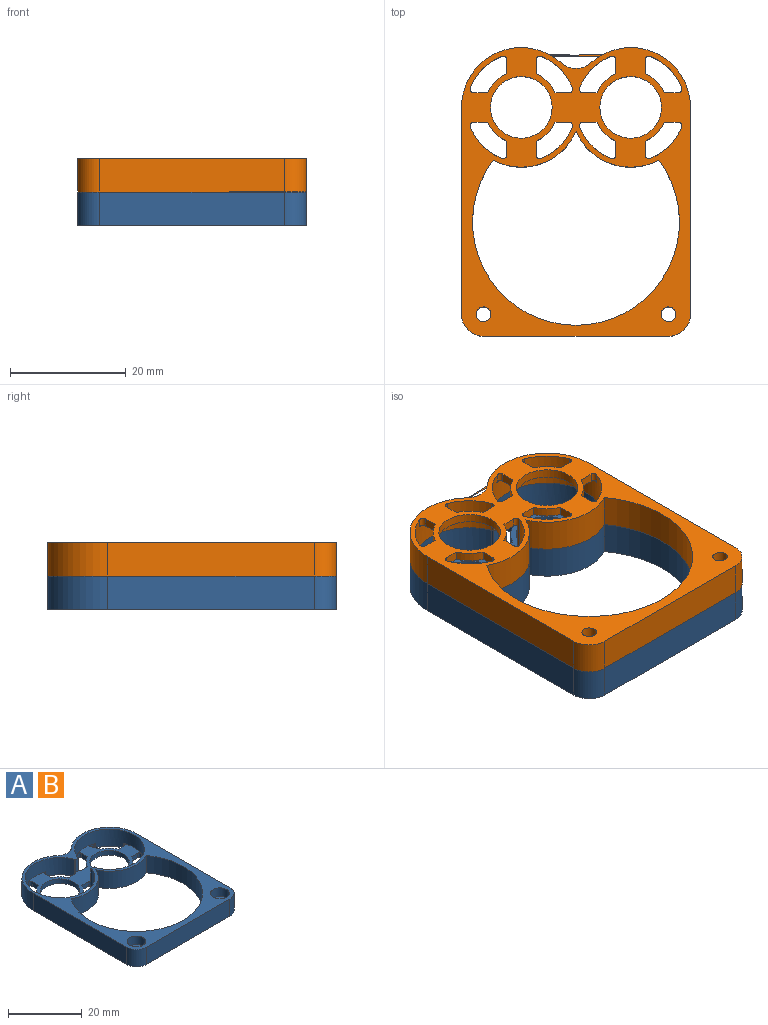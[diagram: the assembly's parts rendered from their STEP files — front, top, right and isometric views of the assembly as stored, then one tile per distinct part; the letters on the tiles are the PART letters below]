
ASSEMBLY  parts=2 mates=1
PART A: 66 faces, bbox 39.6x50x5.7 mm
  f0: cylinder r=9.46mm len=18.92mm, axis (0,0,-1), area 268.1mm2, adj f3,f18,f49,f50,f53,f54,f55,f56
  f1: cylinder r=1.27mm len=2.86mm, axis (0,0,-1), area 22.8mm2, adj f18,f20
  f2: cylinder r=1.27mm len=2.86mm, axis (0,0,-1), area 22.8mm2, adj f18,f22
  f3: plane 49.97x39.62mm, normal (0,0,1), area 431.2mm2, adj f0,f4,f5,f6,f7,f8,f9,f10
  f4: plane 35.81x5.72mm, normal (1,0,0), area 204.7mm2, adj f3,f5,f15,f18
  f5: cylinder r=10.35mm len=17.27mm, axis (0,0,-1), area 136.2mm2, adj f3,f4,f6,f18
  f6: cylinder r=3.81mm len=5.72mm, axis (0,0,-1), area 31.9mm2, adj f3,f5,f7,f18
  f7: cylinder r=10.35mm len=17.27mm, axis (0,0,-1), area 136.2mm2, adj f3,f6,f8,f18
  f8: plane 35.81x5.72mm, normal (-1,0,0), area 204.7mm2, adj f3,f7,f9,f18
  f9: cylinder r=3.81mm len=5.72mm, axis (0,0,-1), area 34.2mm2, adj f3,f8,f10,f18
  f10: plane 32x5.72mm, normal (0,-1,0), area 182.9mm2, adj f3,f9,f15,f18
  f11: cylinder r=10.35mm len=14.36mm, axis (0,0,-1), area 97.4mm2, adj f3,f12,f16,f18
  f12: cylinder r=10.35mm len=14.36mm, axis (0,0,-1), area 97.4mm2, adj f3,f11,f16,f18
  f13: plane 4.19x1.28mm, normal (0,1,0), area 5.4mm2, adj f3,f49,f52,f53
  f14: cylinder r=9.46mm len=18.92mm, axis (0,0,-1), area 268.1mm2, adj f3,f18,f49,f51,f52,f60,f61,f62
  f15: cylinder r=3.81mm len=5.72mm, axis (0,0,-1), area 34.2mm2, adj f3,f4,f10,f18
  f16: cylinder r=17.91mm len=35.81mm, axis (0,0,-1), area 452.5mm2, adj f3,f11,f12,f18
  f17: plane 4.19x1.28mm, normal (0,-1,0), area 5.4mm2, adj f3,f49,f50,f51
  f18: plane 49.97x39.62mm, normal (0,0,-1), area 669.7mm2, adj f0,f1,f2,f4,f5,f6,f7,f8
  f19: cylinder r=2.54mm len=5.08mm, axis (0,0,1), area 45.6mm2, adj f3,f20
  f20: plane 5.08x5.08mm, normal (0,0,1), area 15.2mm2, adj f1,f19
  f21: cylinder r=2.54mm len=5.08mm, axis (0,0,1), area 45.6mm2, adj f3,f22
  f22: plane 5.08x5.08mm, normal (0,0,1), area 15.2mm2, adj f2,f21
  f23: plane 2.42x1.52mm, normal (0,1,0), area 3.7mm2, adj f18,f24,f49,f50
  f24: cylinder r=6.35mm len=3.28mm, axis (0,0,-1), area 7.2mm2, adj f18,f23,f25,f49
  f25: plane 2.42x1.52mm, normal (-1,0,0), area 3.7mm2, adj f18,f24,f49,f54
  f26: plane 2.42x1.52mm, normal (1,0,0), area 3.7mm2, adj f18,f27,f49,f55
  f27: cylinder r=6.35mm len=3.28mm, axis (0,0,-1), area 7.2mm2, adj f18,f26,f28,f49
  f28: plane 2.42x1.52mm, normal (0,1,0), area 3.7mm2, adj f18,f27,f49,f56
  f29: plane 2.42x1.52mm, normal (0,-1,0), area 3.7mm2, adj f18,f30,f49,f57
  f30: cylinder r=6.35mm len=3.28mm, axis (0,0,-1), area 7.2mm2, adj f18,f29,f31,f49
  f31: plane 2.42x1.52mm, normal (1,0,0), area 3.7mm2, adj f18,f30,f49,f58
  f32: plane 2.42x1.52mm, normal (-1,0,0), area 3.7mm2, adj f18,f33,f49,f59
  f33: cylinder r=6.35mm len=3.28mm, axis (0,0,-1), area 7.2mm2, adj f18,f32,f34,f49
  f34: plane 2.42x1.52mm, normal (0,-1,0), area 3.7mm2, adj f18,f33,f49,f53
  f35: plane 2.42x1.52mm, normal (0,-1,0), area 3.7mm2, adj f18,f36,f49,f52
  f36: cylinder r=6.35mm len=3.28mm, axis (0,0,-1), area 7.2mm2, adj f18,f35,f37,f49
  f37: plane 2.42x1.52mm, normal (1,0,0), area 3.7mm2, adj f18,f36,f49,f60
  f38: plane 2.42x1.52mm, normal (-1,0,0), area 3.7mm2, adj f18,f39,f49,f61
  f39: cylinder r=6.35mm len=3.28mm, axis (0,0,-1), area 7.2mm2, adj f18,f38,f40,f49
  f40: plane 2.42x1.52mm, normal (0,-1,0), area 3.7mm2, adj f18,f39,f49,f62
  f41: plane 2.42x1.52mm, normal (0,1,0), area 3.7mm2, adj f18,f42,f49,f63
  f42: cylinder r=6.35mm len=3.28mm, axis (0,0,-1), area 7.2mm2, adj f18,f41,f43,f49
  f43: plane 2.42x1.52mm, normal (-1,0,0), area 3.7mm2, adj f18,f42,f49,f64
  f44: plane 2.42x1.52mm, normal (1,0,0), area 3.7mm2, adj f18,f45,f49,f65
  f45: cylinder r=6.35mm len=3.28mm, axis (0,0,-1), area 7.2mm2, adj f18,f44,f46,f49
  f46: plane 2.42x1.52mm, normal (0,1,0), area 3.7mm2, adj f18,f45,f49,f51
  f47: cylinder r=5.33mm len=10.67mm, axis (0,0,-1), area 51.1mm2, adj f18,f49
  f48: cylinder r=5.33mm len=10.67mm, axis (0,0,-1), area 51.1mm2, adj f18,f49
  f49: plane 37.85x18.92mm, normal (0,0,1), area 208mm2, adj f0,f13,f14,f17,f23,f24,f25,f26
  f50: cylinder r=0.64mm len=5.72mm, axis (0,0,-1), area 3.9mm2, adj f0,f3,f17,f18,f23,f49
  f51: cylinder r=0.64mm len=5.72mm, axis (0,0,-1), area 3.9mm2, adj f3,f14,f17,f18,f46,f49
  f52: cylinder r=0.64mm len=5.72mm, axis (0,0,-1), area 3.9mm2, adj f3,f13,f14,f18,f35,f49
  f53: cylinder r=0.64mm len=5.72mm, axis (0,0,-1), area 3.9mm2, adj f0,f3,f13,f18,f34,f49
  f54: cylinder r=0.64mm len=1.52mm, axis (0,0,-1), area 1.9mm2, adj f0,f18,f25,f49
  f55: cylinder r=0.64mm len=1.52mm, axis (0,0,-1), area 1.9mm2, adj f0,f18,f26,f49
  f56: cylinder r=0.64mm len=1.52mm, axis (0,0,-1), area 1.9mm2, adj f0,f18,f28,f49
  f57: cylinder r=0.64mm len=1.52mm, axis (0,0,-1), area 1.9mm2, adj f0,f18,f29,f49
  f58: cylinder r=0.64mm len=1.52mm, axis (0,0,-1), area 1.9mm2, adj f0,f18,f31,f49
  f59: cylinder r=0.64mm len=1.52mm, axis (0,0,-1), area 1.9mm2, adj f0,f18,f32,f49
  f60: cylinder r=0.64mm len=1.52mm, axis (0,0,-1), area 1.9mm2, adj f14,f18,f37,f49
  f61: cylinder r=0.64mm len=1.52mm, axis (0,0,-1), area 1.9mm2, adj f14,f18,f38,f49
  f62: cylinder r=0.64mm len=1.52mm, axis (0,0,-1), area 1.9mm2, adj f14,f18,f40,f49
  f63: cylinder r=0.64mm len=1.52mm, axis (0,0,-1), area 1.9mm2, adj f14,f18,f41,f49
  f64: cylinder r=0.64mm len=1.52mm, axis (0,0,-1), area 1.9mm2, adj f14,f18,f43,f49
  f65: cylinder r=0.64mm len=1.52mm, axis (0,0,-1), area 1.9mm2, adj f14,f18,f44,f49
PART B: same geometry as A
PLACE A t=(-0.42,-7.93,-6.98)mm
PLACE B rot(axis=(0,1,0),180deg) t=(-0.42,-7.93,4.45)mm
MATE planar B.f3 <-> A.f3  axis (0,0,-1) through (-20.23,-6.03,-1.26)mm
